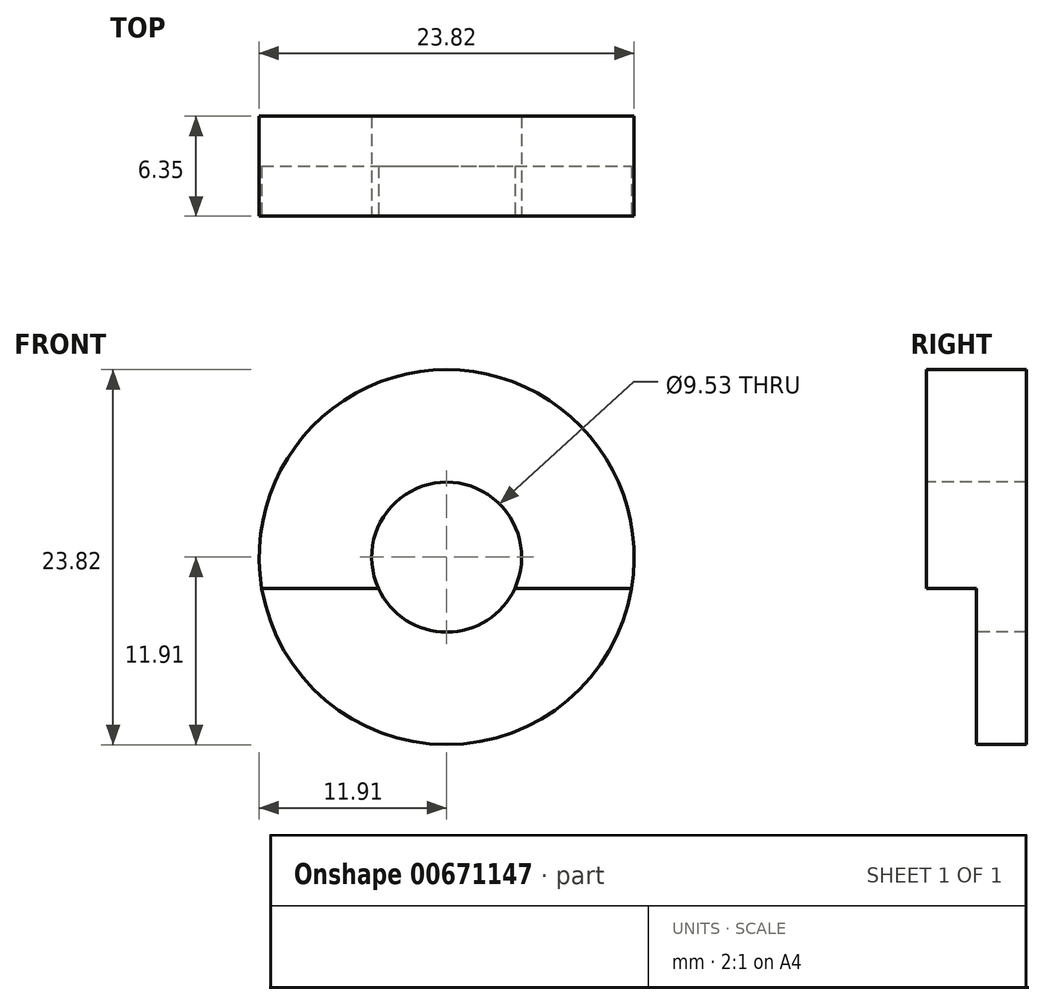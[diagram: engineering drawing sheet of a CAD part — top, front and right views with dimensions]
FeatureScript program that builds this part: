
annotation { "Feature Type Name" : "Feature", "Feature Type Description" : "" }
export const myFeature = defineFeature(function(context is Context, id is Id, definition is map)
    precondition{}
    {
        {
            var Q0;
            Q0=qCreatedBy(makeId("Front.planeOp"),FACE);
            var sketch = newSketch(context, id + "F0", { "sketchPlane" : qUnion([Q0])});
            skCircle(sketch, "E0", {"center": v(0, 0) * mm, "radius": 11.9 * mm});
            skSolve(sketch);
        }
        {
            var Q0;
            Q0=qSketchRegion(id+"F0",true);
            extrude(context, id + "F1", {"entities" : qUnion([Q0]), "depth" : 6.35 * mm});
        }
        {
            var Q0;
            Q0=makeQuery(id+"F1.opExtrude","CAP_FACE",FACE,{"disambiguationData":[OSD([sQuery(id+"F0.wireOp",EDGE,"E0")])],"isStart":false});
            var sketch = newSketch(context, id + "F2", { "sketchPlane" : qUnion([Q0])});
            skCircle(sketch, "E1", {"center": v(0, 0) * mm, "radius": 4.76 * mm});
            skSolve(sketch);
        }
        {
            var Q0;
            Q0=qSketchRegion(id+"F2",true);
            extrude(context, id + "F3", {"entities" : qUnion([Q0]), "operationType" : NewBodyOperationType.REMOVE, "oppositeDirection" : true, "depth" : 25.4 * mm});
        }
        {
            var Q0;
            Q0=makeQuery(id+"F1.opExtrude","CAP_FACE",FACE,{"disambiguationData":[OSD([sQuery(id+"F0.wireOp",EDGE,"E0")])],"isStart":false});
            var sketch = newSketch(context, id + "F4", { "sketchPlane" : qUnion([Q0])});
            skLineSegment(sketch, "E2", {"start": v(-16.23, -1.98) * mm, "end": v(17.4, -1.98) * mm});
            skArc(sketch, "E3", {"start": v(-4.33, -1.98) * mm, "mid": v(0, -4.76) * mm, "end": v(4.33, -1.98) * mm});
            skArc(sketch, "E4", {"start": v(-11.74, -1.98) * mm, "mid": v(0, -11.9) * mm, "end": v(11.74, -1.98) * mm});
            skSolve(sketch);
        }
        {
            var Q0;
            Q0=qSketchRegion(id+"F4",true);
            extrude(context, id + "F5", {"entities" : qUnion([Q0]), "operationType" : NewBodyOperationType.REMOVE, "oppositeDirection" : true, "depth" : 3.17 * mm});
        }
    });
